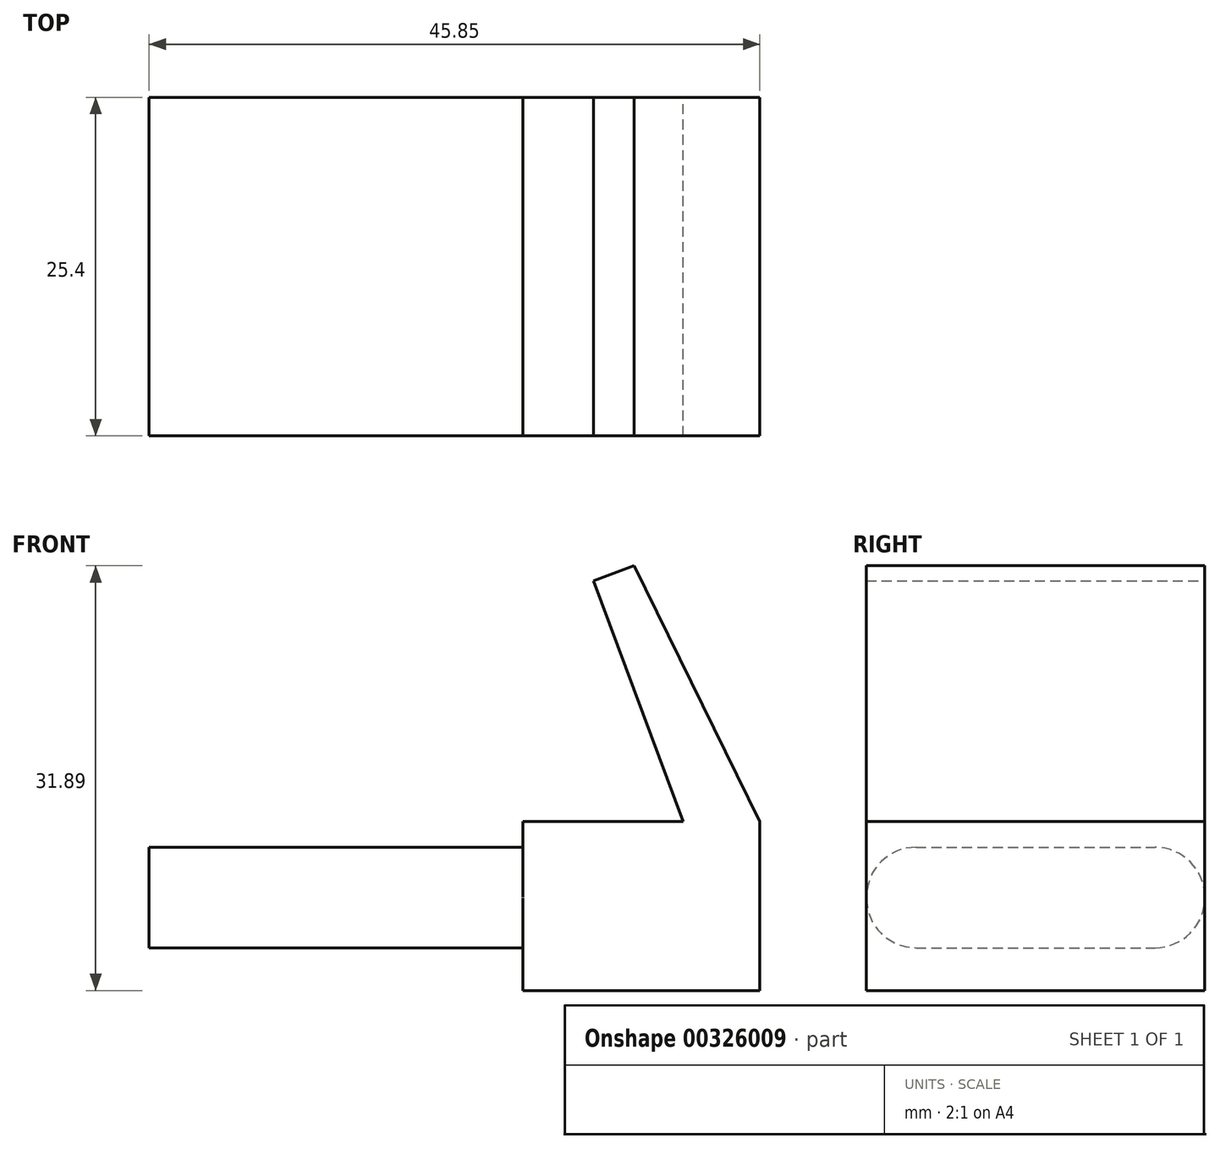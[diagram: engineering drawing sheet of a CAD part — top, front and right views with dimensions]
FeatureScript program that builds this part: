
annotation { "Feature Type Name" : "Feature", "Feature Type Description" : "" }
export const myFeature = defineFeature(function(context is Context, id is Id, definition is map)
    precondition{}
    {
        {
            var Q0;
            Q0=qCreatedBy(makeId("Front.planeOp"),FACE);
            var sketch = newSketch(context, id + "F0", { "sketchPlane" : qUnion([Q0])});
            skLineSegment(sketch, "E0", {"start": v(-33.35, -3.14) * mm, "end": v(-33.35, 4.4) * mm});
            skLineSegment(sketch, "E1", {"start": v(-33.35, 4.4) * mm, "end": v(-5.28, 4.4) * mm});
            skLineSegment(sketch, "E2", {"start": v(-5.28, 4.4) * mm, "end": v(-5.28, 6.35) * mm});
            skLineSegment(sketch, "E3", {"start": v(-5.28, 6.35) * mm, "end": v(6.75, 6.35) * mm});
            skLineSegment(sketch, "E4", {"start": v(6.75, 6.35) * mm, "end": v(0, 24.4) * mm});
            skLineSegment(sketch, "E5", {"start": v(0, 24.4) * mm, "end": v(3.06, 25.54) * mm});
            skLineSegment(sketch, "E6", {"start": v(3.06, 25.54) * mm, "end": v(12.5, 6.35) * mm});
            skLineSegment(sketch, "E7", {"start": v(12.5, 6.35) * mm, "end": v(12.5, -6.35) * mm});
            skLineSegment(sketch, "E8", {"start": v(12.5, -6.35) * mm, "end": v(-5.28, -6.35) * mm});
            skLineSegment(sketch, "E9", {"start": v(-5.28, -6.35) * mm, "end": v(-5.28, -3.14) * mm});
            skLineSegment(sketch, "E10", {"start": v(-5.28, -3.14) * mm, "end": v(-33.35, -3.14) * mm});
            skSolve(sketch);
        }
        {
            var Q0;
            Q0=makeQuery(id+"F0.imprint","IMPRINT",FACE,{"disambiguationData":[TD([[makeQuery(id+"F0.imprint","IMPRINT",EDGE,{"derivedFrom":sQuery(id+"F0.wireOp",EDGE,"E0")}),-1.0]])]});
            extrude(context, id + "F1", {"entities" : qUnion([Q0]), "depth" : 25.4 * mm});
        }
        {
            var Q0;
            Q0=makeQuery(id+"F1.opExtrude","CAP_EDGE",EDGE,{"disambiguationData":[OSD([sQuery(id+"F0.wireOp",EDGE,"E1")])],"isStart":false});
            var Q1;
            Q1=makeQuery(id+"F1.opExtrude","CAP_EDGE",EDGE,{"disambiguationData":[OSD([sQuery(id+"F0.wireOp",EDGE,"E10")])],"isStart":false});
            var Q2;
            Q2=makeQuery(id+"F1.opExtrude","CAP_EDGE",EDGE,{"disambiguationData":[OSD([sQuery(id+"F0.wireOp",EDGE,"E1")])],"isStart":true});
            var Q3;
            Q3=makeQuery(id+"F1.opExtrude","CAP_EDGE",EDGE,{"disambiguationData":[OSD([sQuery(id+"F0.wireOp",EDGE,"E10")])],"isStart":true});
            fillet(context, id + "F2", {"entities" : qUnion([Q0, Q1, Q2, Q3]), "radius" : 3.73 * mm, "tangentPropagation" : true, "allowEdgeOverflow" : false});
        }
    });
